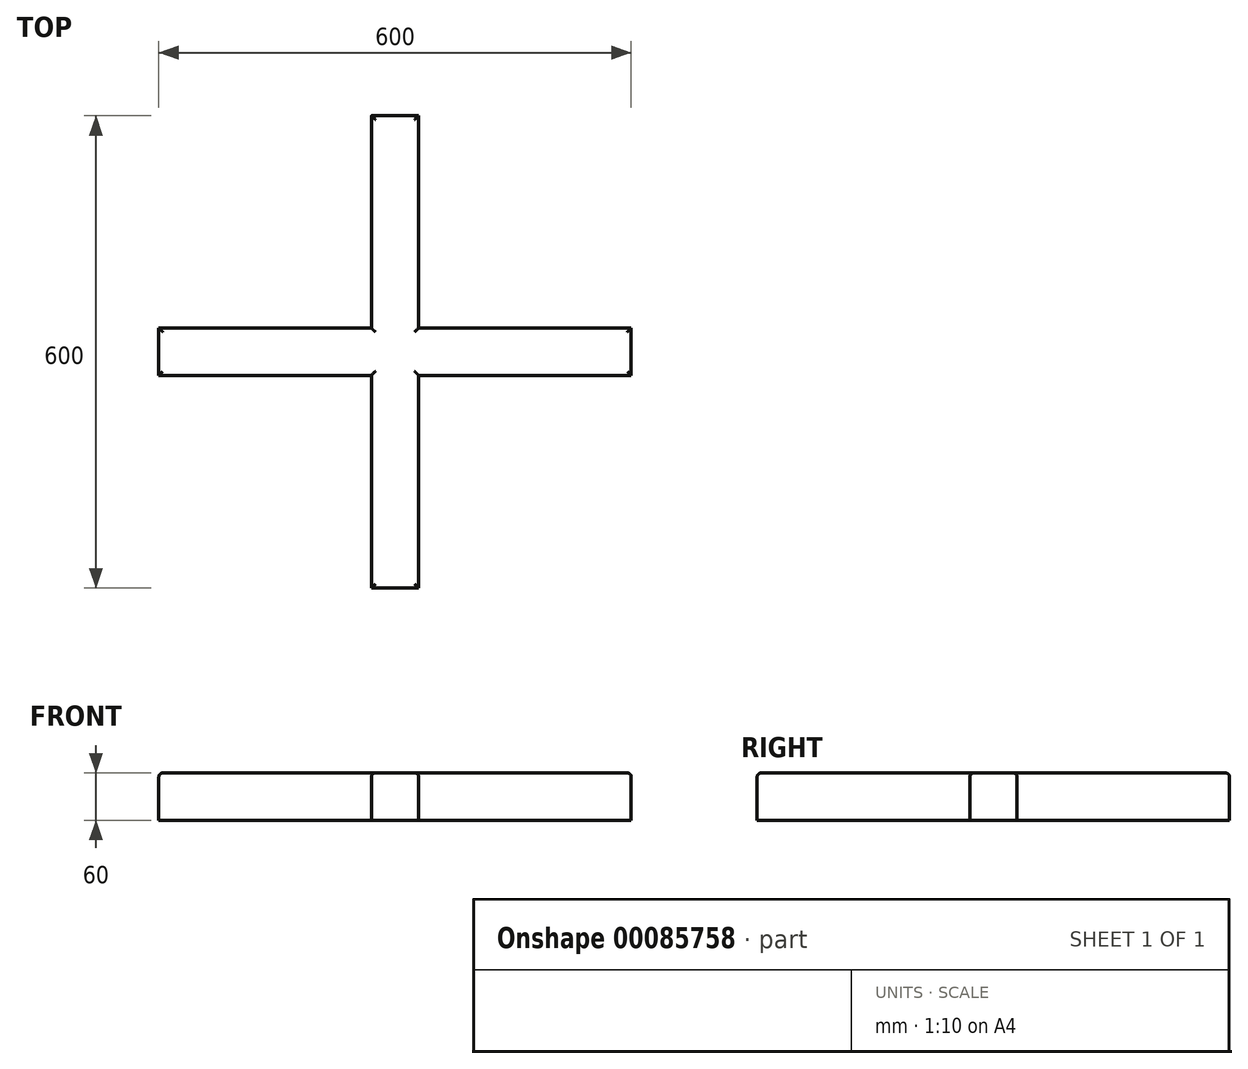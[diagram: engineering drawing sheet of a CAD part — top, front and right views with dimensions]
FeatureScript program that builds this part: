
annotation { "Feature Type Name" : "Feature", "Feature Type Description" : "" }
export const myFeature = defineFeature(function(context is Context, id is Id, definition is map)
    precondition{}
    {
        {
            var Q0;
            Q0=qCreatedBy(makeId("Top.planeOp"),FACE);
            var sketch = newSketch(context, id + "F0", { "sketchPlane" : qUnion([Q0])});
            skLineSegment(sketch, "E0.bottom", {"start": v(-300, 30.22) * mm, "end": v(-30, 30.22) * mm});
            skLineSegment(sketch, "E0.top", {"start": v(-300, -29.78) * mm, "end": v(-30, -29.78) * mm});
            skLineSegment(sketch, "E0.left", {"start": v(-300, 30.22) * mm, "end": v(-300, -29.78) * mm});
            skLineSegment(sketch, "E0.right", {"start": v(300, 30.22) * mm, "end": v(300, -29.78) * mm});
            skLineSegment(sketch, "E1.bottom", {"start": v(30, -300) * mm, "end": v(-30, -300) * mm});
            skLineSegment(sketch, "E1.top", {"start": v(30, 300) * mm, "end": v(-30, 300) * mm});
            skLineSegment(sketch, "E1.left", {"start": v(30, -300) * mm, "end": v(30, -29.78) * mm});
            skLineSegment(sketch, "E1.right", {"start": v(-30, -300) * mm, "end": v(-30, -29.78) * mm});
            skLineSegment(sketch, "E2.trimOffspring", {"start": v(30, 30.22) * mm, "end": v(300, 30.22) * mm});
            skLineSegment(sketch, "E3.trimOffspring", {"start": v(-30, 30.22) * mm, "end": v(-30, 300) * mm});
            skLineSegment(sketch, "E4.trimOffspring", {"start": v(30, 30.22) * mm, "end": v(30, 300) * mm});
            skLineSegment(sketch, "E5.trimOffspring", {"start": v(30, -29.78) * mm, "end": v(300, -29.78) * mm});
            skSolve(sketch);
        }
        {
            var Q0;
            Q0=makeQuery(id+"F0.imprint","IMPRINT",FACE,{"disambiguationData":[TD([[makeQuery(id+"F0.imprint","IMPRINT",EDGE,{"derivedFrom":sQuery(id+"F0.wireOp",EDGE,"E0.bottom")}),-1.0]])]});
            extrude(context, id + "F1", {"entities" : qUnion([Q0]), "depth" : 60 * mm});
        }
        {
            var Q0;
            Q0=makeQuery(id+"F1.opExtrude","CAP_FACE",FACE,{"disambiguationData":[OSD([sQuery(id+"F0.wireOp",EDGE,"E0.bottom"),sQuery(id+"F0.wireOp",EDGE,"E0.top"),sQuery(id+"F0.wireOp",EDGE,"E0.left"),sQuery(id+"F0.wireOp",EDGE,"E0.right"),sQuery(id+"F0.wireOp",EDGE,"E1.bottom"),sQuery(id+"F0.wireOp",EDGE,"E1.top"),sQuery(id+"F0.wireOp",EDGE,"E1.left"),sQuery(id+"F0.wireOp",EDGE,"E1.right"),sQuery(id+"F0.wireOp",EDGE,"E2.trimOffspring"),sQuery(id+"F0.wireOp",EDGE,"E3.trimOffspring"),sQuery(id+"F0.wireOp",EDGE,"E4.trimOffspring"),sQuery(id+"F0.wireOp",EDGE,"E5.trimOffspring")])],"isStart":false});
            fillet(context, id + "F2", {"entities" : qUnion([Q0]), "radius" : 5 * mm, "tangentPropagation" : true, "allowEdgeOverflow" : false});
        }
    });
